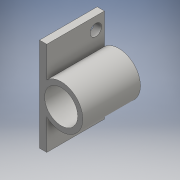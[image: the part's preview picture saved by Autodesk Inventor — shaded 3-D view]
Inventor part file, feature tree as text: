
AUTODESK INVENTOR PART (.ipt)
format: ipt  version: 2016 (Build 200138000, 138)  size: 118,272 bytes
history: native  units: mm
features: extrude x2, sketch x2
ambient origin geometry x8: Origin, YZ Plane, XZ Plane, XY Plane, X Axis, Y Axis, Z Axis, Center Point
bodies: Solid1 (feature_tree)
feature tree (4):
  extrude  "Extrusion1"  Depth=26.0mm
  extrude  "Extrusion2"  Depth=16.0mm TaperAngle=0.0deg
  sketch  "Sketch1"  dims[d0=9.2mm d2=26.0mm]
  sketch  "Sketch2"  dims[d3=2.0mm d4=16.0mm d5=0.0mm d10=3.2mm d11=3.2mm d12=16.0mm d13=0.0mm d14=2.4mm d15=2.4mm]
